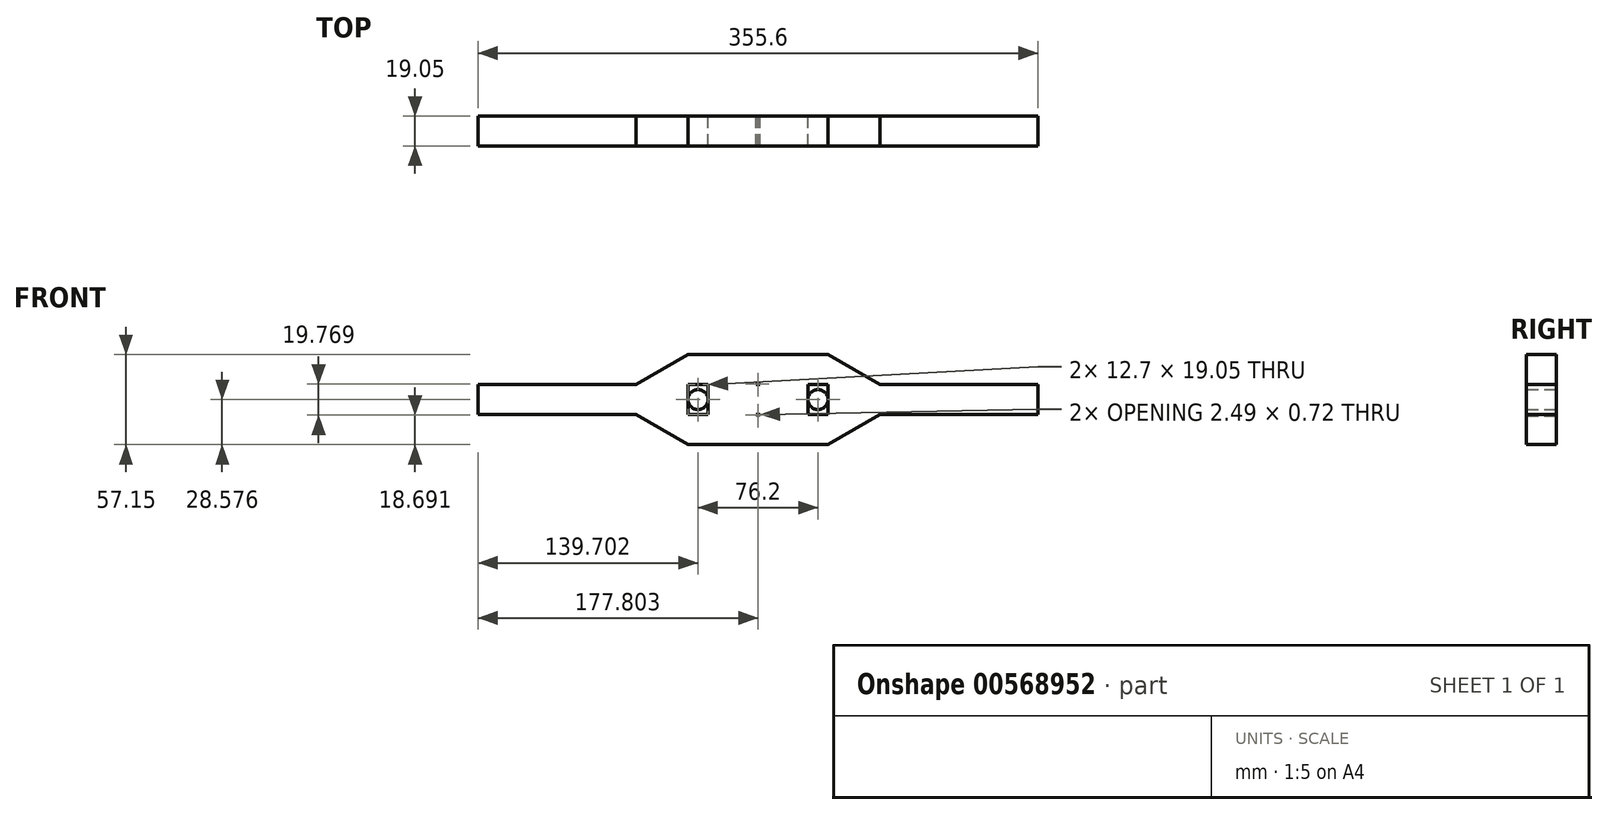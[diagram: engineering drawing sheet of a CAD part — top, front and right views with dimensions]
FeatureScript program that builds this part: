
annotation { "Feature Type Name" : "Feature", "Feature Type Description" : "" }
export const myFeature = defineFeature(function(context is Context, id is Id, definition is map)
    precondition{}
    {
        {
            var Q0;
            Q0=qCreatedBy(makeId("Front.planeOp"),FACE);
            var sketch = newSketch(context, id + "F0", { "sketchPlane" : qUnion([Q0])});
            skLineSegment(sketch, "E0.bottom", {"start": v(-180.66, -65.79) * mm, "end": v(174.94, -65.79) * mm});
            skLineSegment(sketch, "E0.top", {"start": v(-180.66, -84.84) * mm, "end": v(174.94, -84.84) * mm});
            skLineSegment(sketch, "E0.left", {"start": v(-180.66, -65.79) * mm, "end": v(-180.66, -84.84) * mm});
            skLineSegment(sketch, "E0.right", {"start": v(174.94, -65.79) * mm, "end": v(174.94, -84.84) * mm});
            skLineSegment(sketch, "E1", {"start": v(-2.86, -65.79) * mm, "end": v(-2.86, -84.84) * mm});
            skLineSegment(sketch, "E2", {"start": v(-40.96, -65.79) * mm, "end": v(-40.96, -84.84) * mm});
            skLineSegment(sketch, "E3", {"start": v(35.24, -65.79) * mm, "end": v(35.24, -84.84) * mm});
            skCircle(sketch, "E4", {"center": v(-40.96, -75.31) * mm, "radius": 6.35 * mm});
            skCircle(sketch, "E5", {"center": v(35.24, -75.31) * mm, "radius": 6.35 * mm});
            skLineSegment(sketch, "E6.bottom", {"start": v(-43.38, -84.84) * mm, "end": v(-34.6, -84.84) * mm});
            skLineSegment(sketch, "E7", {"start": v(-47.3, -65.79) * mm, "end": v(-47.3, -84.84) * mm});
            skLineSegment(sketch, "E8", {"start": v(-34.6, -65.79) * mm, "end": v(-34.6, -84.84) * mm});
            skLineSegment(sketch, "E9", {"start": v(28.9, -65.79) * mm, "end": v(28.9, -84.84) * mm});
            skLineSegment(sketch, "E10", {"start": v(41.6, -65.79) * mm, "end": v(41.6, -84.84) * mm});
            skLineSegment(sketch, "E11.bottom", {"start": v(-47.3, -65.79) * mm, "end": v(-34.6, -65.79) * mm});
            skLineSegment(sketch, "E11.top", {"start": v(-47.3, -46.74) * mm, "end": v(-34.6, -46.74) * mm});
            skLineSegment(sketch, "E11.left", {"start": v(-47.3, -65.79) * mm, "end": v(-47.3, -46.74) * mm});
            skLineSegment(sketch, "E11.right", {"start": v(-34.6, -65.79) * mm, "end": v(-34.6, -46.74) * mm});
            skLineSegment(sketch, "E12.bottom", {"start": v(-34.6, -84.84) * mm, "end": v(-47.3, -84.84) * mm});
            skLineSegment(sketch, "E12.top", {"start": v(-34.6, -103.89) * mm, "end": v(-47.3, -103.89) * mm});
            skLineSegment(sketch, "E12.left", {"start": v(-34.6, -84.84) * mm, "end": v(-34.6, -103.89) * mm});
            skLineSegment(sketch, "E12.right", {"start": v(-47.3, -84.84) * mm, "end": v(-47.3, -103.89) * mm});
            skLineSegment(sketch, "E13.bottom", {"start": v(28.9, -84.84) * mm, "end": v(41.6, -84.84) * mm});
            skLineSegment(sketch, "E13.top", {"start": v(28.9, -103.89) * mm, "end": v(41.6, -103.89) * mm});
            skLineSegment(sketch, "E13.left", {"start": v(28.9, -84.84) * mm, "end": v(28.9, -103.89) * mm});
            skLineSegment(sketch, "E13.right", {"start": v(41.6, -84.84) * mm, "end": v(41.6, -103.89) * mm});
            skLineSegment(sketch, "E14.bottom", {"start": v(28.9, -65.79) * mm, "end": v(41.6, -65.79) * mm});
            skLineSegment(sketch, "E14.top", {"start": v(28.9, -46.74) * mm, "end": v(41.6, -46.74) * mm});
            skLineSegment(sketch, "E14.left", {"start": v(28.9, -65.79) * mm, "end": v(28.9, -46.74) * mm});
            skLineSegment(sketch, "E14.right", {"start": v(41.6, -65.79) * mm, "end": v(41.6, -46.74) * mm});
            skLineSegment(sketch, "E15", {"start": v(-47.3, -46.74) * mm, "end": v(-80.3, -65.79) * mm});
            skLineSegment(sketch, "E16", {"start": v(-34.6, -46.74) * mm, "end": v(-1.61, -65.79) * mm});
            skLineSegment(sketch, "E17", {"start": v(-47.3, -103.89) * mm, "end": v(-80.3, -84.84) * mm});
            skLineSegment(sketch, "E18", {"start": v(-34.6, -103.89) * mm, "end": v(-1.61, -84.84) * mm});
            skLineSegment(sketch, "E19", {"start": v(28.9, -46.74) * mm, "end": v(-4.1, -65.79) * mm});
            skLineSegment(sketch, "E20", {"start": v(41.6, -46.74) * mm, "end": v(74.59, -65.79) * mm});
            skLineSegment(sketch, "E21", {"start": v(41.6, -103.89) * mm, "end": v(74.59, -84.84) * mm});
            skLineSegment(sketch, "E22", {"start": v(28.9, -103.89) * mm, "end": v(-4.1, -84.84) * mm});
            skLineSegment(sketch, "E23", {"start": v(-34.6, -46.74) * mm, "end": v(28.9, -46.74) * mm});
            skLineSegment(sketch, "E24", {"start": v(-34.6, -103.89) * mm, "end": v(28.9, -103.89) * mm});
            skSolve(sketch);
        }
        {
            var Q0;
            Q0=makeQuery(id+"F0.imprint","IMPRINT",FACE,{"disambiguationData":[TD([[makeQuery(id+"F0.imprint","IMPRINT",EDGE,{"derivedFrom":sQuery(id+"F0.wireOp",EDGE,"E0.bottom")}),-1.0]])]});
            var Q1;
            {var subQ0=sQuery(id+"F0.wireOp",EDGE,"E11.bottom");var subQ1=sQuery(id+"F0.wireOp",EDGE,"E2");var subQ2=makeQuery(id+"F0.imprint","INTERSECT",VERTEX,{"derivedFrom":[subQ1,subQ0]});Q1=makeQuery(id+"F0.imprint","IMPRINT",FACE,{"disambiguationData":[TD([[makeQuery(id+"F0.imprint","IMPRINT",EDGE,{"disambiguationData":[TD([[subQ2,-1.0]])],"derivedFrom":subQ1}),-1.0]])]});}
            var Q2;
            Q2=makeQuery(id+"F0.imprint","IMPRINT",FACE,{"disambiguationData":[TD([[makeQuery(id+"F0.imprint","IMPRINT",EDGE,{"derivedFrom":sQuery(id+"F0.wireOp",EDGE,"E11.top")}),-1.0]])]});
            var Q3;
            {var subQ0=sQuery(id+"F0.wireOp",EDGE,"E11.left");Q3=makeQuery(id+"F0.imprint","IMPRINT",FACE,{"disambiguationData":[TD([[makeQuery(id+"F0.imprint","IMPRINT",EDGE,{"derivedFrom":subQ0}),1.0]])]});}
            var Q4;
            {var subQ0=sQuery(id+"F0.wireOp",EDGE,"E11.right");Q4=makeQuery(id+"F0.imprint","IMPRINT",FACE,{"disambiguationData":[TD([[makeQuery(id+"F0.imprint","IMPRINT",EDGE,{"derivedFrom":subQ0}),-1.0]])]});}
            var Q5;
            {var subQ0=sQuery(id+"F0.wireOp",EDGE,"E23");Q5=makeQuery(id+"F0.imprint","IMPRINT",FACE,{"disambiguationData":[TD([[makeQuery(id+"F0.imprint","IMPRINT",EDGE,{"derivedFrom":subQ0}),-1.0]])]});}
            var Q6;
            Q6=makeQuery(id+"F0.imprint","IMPRINT",FACE,{"disambiguationData":[TD([[makeQuery(id+"F0.imprint","IMPRINT",EDGE,{"derivedFrom":sQuery(id+"F0.wireOp",EDGE,"E14.top")}),-1.0]])]});
            var Q7;
            {var subQ0=sQuery(id+"F0.wireOp",EDGE,"E14.right");Q7=makeQuery(id+"F0.imprint","IMPRINT",FACE,{"disambiguationData":[TD([[makeQuery(id+"F0.imprint","IMPRINT",EDGE,{"derivedFrom":subQ0}),-1.0]])]});}
            var Q8;
            {var subQ0=sQuery(id+"F0.wireOp",EDGE,"E11.bottom");var subQ1=sQuery(id+"F0.wireOp",EDGE,"E2");var subQ2=makeQuery(id+"F0.imprint","INTERSECT",VERTEX,{"derivedFrom":[subQ1,subQ0]});Q8=makeQuery(id+"F0.imprint","IMPRINT",FACE,{"disambiguationData":[TD([[makeQuery(id+"F0.imprint","IMPRINT",EDGE,{"disambiguationData":[TD([[subQ2,-1.0]])],"derivedFrom":subQ1}),1.0]])]});}
            var Q9;
            {var subQ0=sQuery(id+"F0.wireOp",EDGE,"E14.left");Q9=makeQuery(id+"F0.imprint","IMPRINT",FACE,{"disambiguationData":[TD([[makeQuery(id+"F0.imprint","IMPRINT",EDGE,{"derivedFrom":subQ0}),1.0]])]});}
            var Q10;
            {var subQ0=sQuery(id+"F0.wireOp",EDGE,"E13.left");Q10=makeQuery(id+"F0.imprint","IMPRINT",FACE,{"disambiguationData":[TD([[makeQuery(id+"F0.imprint","IMPRINT",EDGE,{"derivedFrom":subQ0}),-1.0]])]});}
            var Q11;
            {var subQ0=sQuery(id+"F0.wireOp",EDGE,"E24");Q11=makeQuery(id+"F0.imprint","IMPRINT",FACE,{"disambiguationData":[TD([[makeQuery(id+"F0.imprint","IMPRINT",EDGE,{"derivedFrom":subQ0}),1.0]])]});}
            var Q12;
            {var subQ0=sQuery(id+"F0.wireOp",EDGE,"E12.left");Q12=makeQuery(id+"F0.imprint","IMPRINT",FACE,{"disambiguationData":[TD([[makeQuery(id+"F0.imprint","IMPRINT",EDGE,{"derivedFrom":subQ0}),1.0]])]});}
            var Q13;
            {var subQ0=sQuery(id+"F0.wireOp",EDGE,"E12.right");Q13=makeQuery(id+"F0.imprint","IMPRINT",FACE,{"disambiguationData":[TD([[makeQuery(id+"F0.imprint","IMPRINT",EDGE,{"derivedFrom":subQ0}),-1.0]])]});}
            var Q14;
            Q14=makeQuery(id+"F0.imprint","IMPRINT",FACE,{"disambiguationData":[TD([[makeQuery(id+"F0.imprint","IMPRINT",EDGE,{"derivedFrom":sQuery(id+"F0.wireOp",EDGE,"E12.top")}),-1.0]])]});
            var Q15;
            {var subQ0=sQuery(id+"F0.wireOp",EDGE,"E12.bottom");var subQ1=sQuery(id+"F0.wireOp",EDGE,"E2");var subQ2=makeQuery(id+"F0.imprint","INTERSECT",VERTEX,{"derivedFrom":[subQ1,subQ0]});Q15=makeQuery(id+"F0.imprint","IMPRINT",FACE,{"disambiguationData":[TD([[makeQuery(id+"F0.imprint","IMPRINT",EDGE,{"disambiguationData":[TD([[subQ2,1.0]])],"derivedFrom":subQ1}),1.0]])]});}
            var Q16;
            {var subQ0=sQuery(id+"F0.wireOp",EDGE,"E12.bottom");var subQ7=makeQuery(id+"F0.imprint","IMPRINT",VERTEX,{"derivedFrom":subQ0});Q16=makeQuery(id+"F0.imprint","IMPRINT",FACE,{"disambiguationData":[TD([[makeQuery(id+"F0.imprint","IMPRINT",EDGE,{"disambiguationData":[TD([[subQ7,1.0]])],"derivedFrom":subQ0}),-1.0]])]});}
            var Q17;
            {var subQ0=sQuery(id+"F0.wireOp",EDGE,"E13.bottom");var subQ1=sQuery(id+"F0.wireOp",EDGE,"E3");var subQ2=makeQuery(id+"F0.imprint","INTERSECT",VERTEX,{"derivedFrom":[subQ1,subQ0]});Q17=makeQuery(id+"F0.imprint","IMPRINT",FACE,{"disambiguationData":[TD([[makeQuery(id+"F0.imprint","IMPRINT",EDGE,{"disambiguationData":[TD([[subQ2,1.0]])],"derivedFrom":subQ1}),-1.0]])]});}
            var Q18;
            {var subQ0=sQuery(id+"F0.wireOp",EDGE,"E13.bottom");var subQ1=sQuery(id+"F0.wireOp",EDGE,"E3");var subQ2=makeQuery(id+"F0.imprint","INTERSECT",VERTEX,{"derivedFrom":[subQ1,subQ0]});Q18=makeQuery(id+"F0.imprint","IMPRINT",FACE,{"disambiguationData":[TD([[makeQuery(id+"F0.imprint","IMPRINT",EDGE,{"disambiguationData":[TD([[subQ2,1.0]])],"derivedFrom":subQ1}),1.0]])]});}
            var Q19;
            {var subQ0=sQuery(id+"F0.wireOp",EDGE,"E14.bottom");var subQ1=sQuery(id+"F0.wireOp",EDGE,"E3");var subQ2=makeQuery(id+"F0.imprint","INTERSECT",VERTEX,{"derivedFrom":[subQ1,subQ0]});Q19=makeQuery(id+"F0.imprint","IMPRINT",FACE,{"disambiguationData":[TD([[makeQuery(id+"F0.imprint","IMPRINT",EDGE,{"disambiguationData":[TD([[subQ2,-1.0]])],"derivedFrom":subQ1}),1.0]])]});}
            var Q20;
            {var subQ0=sQuery(id+"F0.wireOp",EDGE,"E14.bottom");var subQ1=sQuery(id+"F0.wireOp",EDGE,"E3");var subQ2=makeQuery(id+"F0.imprint","INTERSECT",VERTEX,{"derivedFrom":[subQ1,subQ0]});Q20=makeQuery(id+"F0.imprint","IMPRINT",FACE,{"disambiguationData":[TD([[makeQuery(id+"F0.imprint","IMPRINT",EDGE,{"disambiguationData":[TD([[subQ2,-1.0]])],"derivedFrom":subQ1}),-1.0]])]});}
            var Q21;
            Q21=makeQuery(id+"F0.imprint","IMPRINT",FACE,{"disambiguationData":[TD([[makeQuery(id+"F0.imprint","IMPRINT",EDGE,{"derivedFrom":sQuery(id+"F0.wireOp",EDGE,"E13.top")}),1.0]])]});
            var Q22;
            {var subQ0=sQuery(id+"F0.wireOp",EDGE,"E13.right");Q22=makeQuery(id+"F0.imprint","IMPRINT",FACE,{"disambiguationData":[TD([[makeQuery(id+"F0.imprint","IMPRINT",EDGE,{"derivedFrom":subQ0}),1.0]])]});}
            extrude(context, id + "F1", {"entities" : qUnion([Q0, Q1, Q2, Q3, Q4, Q5, Q6, Q7, Q8, Q9, Q10, Q11, Q12, Q13, Q14, Q15, Q16, Q17, Q18, Q19, Q20, Q21, Q22]), "depth" : 19.05 * mm, "offsetDistance" : 25.4 * mm});
        }
    });
